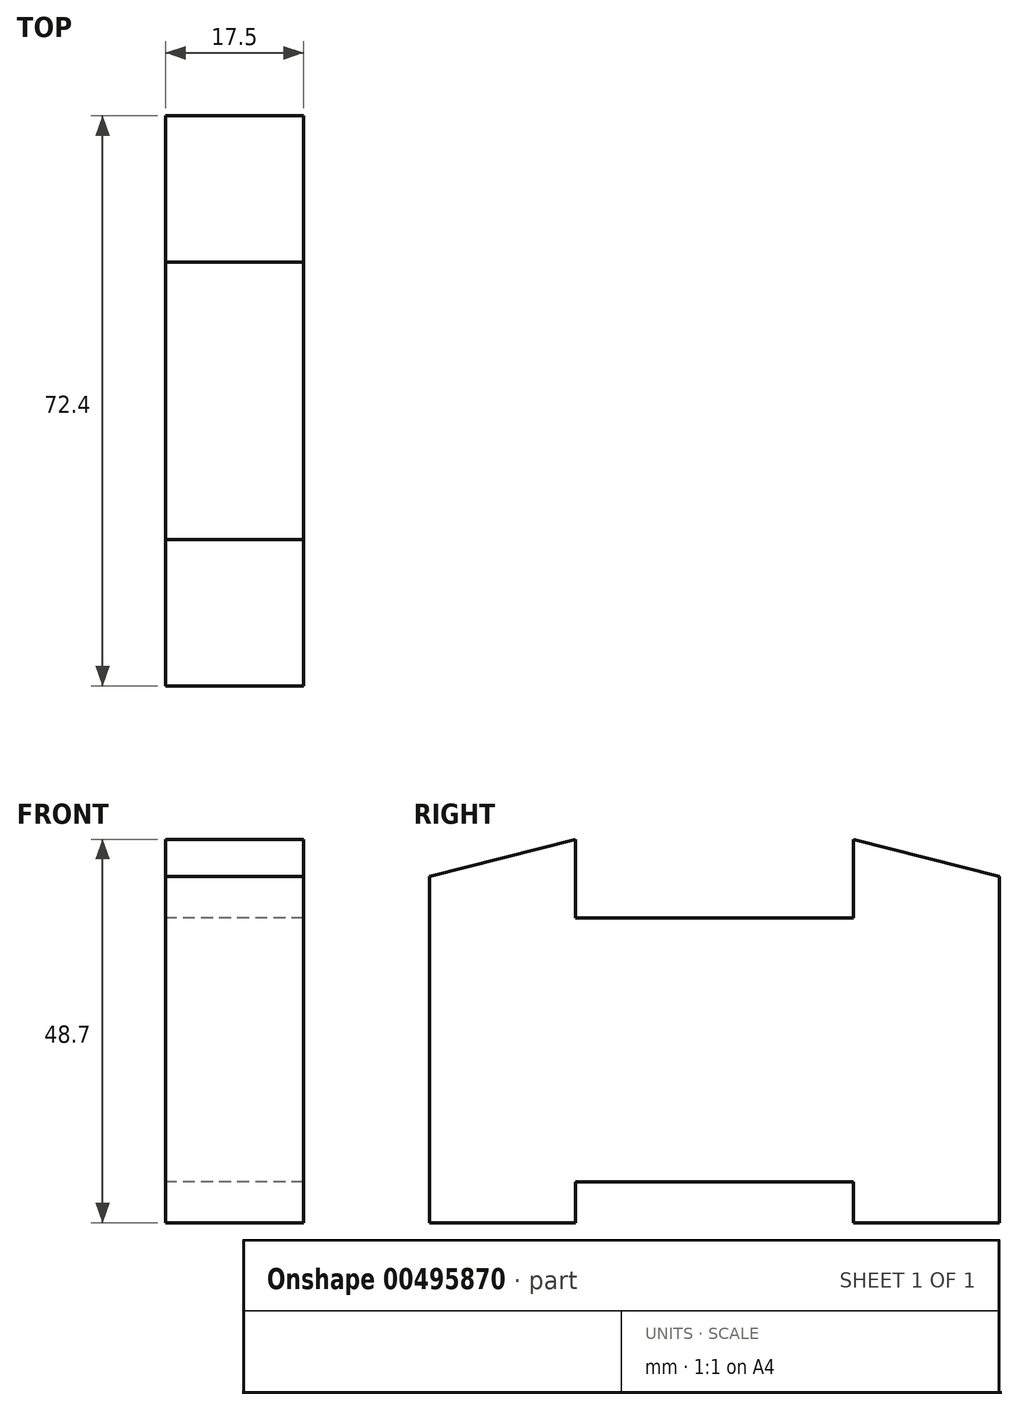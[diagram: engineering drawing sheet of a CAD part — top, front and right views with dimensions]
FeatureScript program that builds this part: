
annotation { "Feature Type Name" : "Feature", "Feature Type Description" : "" }
export const myFeature = defineFeature(function(context is Context, id is Id, definition is map)
    precondition{}
    {
        {
            var Q0;
            Q0=qCreatedBy(makeId("Right.planeOp"),FACE);
            var sketch = newSketch(context, id + "F0", { "sketchPlane" : qUnion([Q0])});
            skLineSegment(sketch, "E0", {"start": v(-36.2, -5.2) * mm, "end": v(-17.65, -5.2) * mm});
            skLineSegment(sketch, "E1", {"start": v(-17.65, -5.2) * mm, "end": v(-17.65, 0) * mm});
            skLineSegment(sketch, "E2", {"start": v(-17.65, 0) * mm, "end": v(17.65, 0) * mm});
            skLineSegment(sketch, "E3", {"start": v(17.65, 0) * mm, "end": v(17.65, -5.2) * mm});
            skLineSegment(sketch, "E4", {"start": v(17.65, -5.2) * mm, "end": v(36.2, -5.2) * mm});
            skLineSegment(sketch, "E5", {"start": v(36.2, -5.2) * mm, "end": v(36.2, 38.8) * mm});
            skLineSegment(sketch, "E6", {"start": v(36.2, 38.8) * mm, "end": v(17.65, 43.5) * mm});
            skLineSegment(sketch, "E7", {"start": v(17.65, 43.5) * mm, "end": v(17.65, 33.5) * mm});
            skLineSegment(sketch, "E8", {"start": v(17.65, 33.5) * mm, "end": v(-17.65, 33.5) * mm});
            skLineSegment(sketch, "E9", {"start": v(-17.65, 33.5) * mm, "end": v(-17.65, 43.5) * mm});
            skLineSegment(sketch, "E10", {"start": v(-17.65, 43.5) * mm, "end": v(-36.2, 38.8) * mm});
            skLineSegment(sketch, "E11", {"start": v(-36.2, 38.8) * mm, "end": v(-36.2, -5.2) * mm});
            skLineSegment(sketch, "E12", {"start": v(-17.65, 33.5) * mm, "end": v(-17.65, 0) * mm, "construction": true});
            skLineSegment(sketch, "E13", {"start": v(17.65, 33.5) * mm, "end": v(17.65, 0) * mm, "construction": true});
            skSolve(sketch);
        }
        {
            var Q0;
            Q0=makeQuery(id+"F0.imprint","IMPRINT",FACE,{"disambiguationData":[TD([[makeQuery(id+"F0.imprint","IMPRINT",EDGE,{"derivedFrom":sQuery(id+"F0.wireOp",EDGE,"E0")}),1.0]])]});
            extrude(context, id + "F1", {"entities" : qUnion([Q0]), "depth" : 17.5 * mm});
        }
    });
